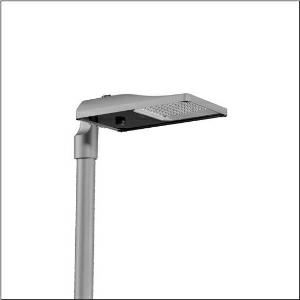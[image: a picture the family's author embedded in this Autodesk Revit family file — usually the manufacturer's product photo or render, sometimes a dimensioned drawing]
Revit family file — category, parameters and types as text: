
# Revit family: streetlight_sl_31_midi___st0_5a_5xh7b4at08la_3b68
name_source: partatom
category: Lighting Fixtures
units: mm (PartAtom-declared; Revit-internal decimal feet)

## family parameters
Cut with Voids When Loaded = No
Host = Face
Light Source = No
Part Type = Normal
Room Calculation Point = No
Round Connector Dimension = Use Diameter
Shared = No

## types (1)
- --- (1 x LED, 13610 lm, 86.5 W, 4000K)
    Apparent Load = 87 VA
    CIE Flux Codes = 41 75 97 100 100
    Color Rendering = 70
    Color Temperature = 4000K
    Default Elevation = 1800 mm
    Description = Streetlight SL 31 midi D4i mast luminaire for post-top, side-entry; light control with lens of PMMA; light distribution: ST0.5a, direct asymmetric distribution, for standard-compliant lighting for roads and squares; LED: luminous flux: 13.610lm, light colour: 740, colour temperature: 4000K; luminous efficacy: 157,3lm/W; control: pre-setting: logarithmic dimming characteristic, flexible luminous flux parameterisation, time-dependent luminous flux control, constant luminous flux control, power reduction, intelligent temperature release in ECG and LED module, overheat protection; luminaire housing, of diecast aluminium, Siteco® metallic grey (DB 702S), corrosivity category C5 high according to DIN EN ISO 12944; cover of toughened safety glass, transparent, opened without tools; mast flange of diecast aluminium, Siteco® metallic grey (DB 702S), spigot size: 76/60mm, mast flange included unmounted; with cable H07RN-F 2x 1.5mm², cable length: 10,5m, connection cable pre-assembled; mains connection: 220..240V, AC, 50/60Hz; power consumption (at start of service life): 86,5W / (at end of service life): 90W / (with reduced operation 50%): 39,6W; protection rating (complete): IP66; insulation class (complete): insulation class II (safety insulation); impact resistance: IK09; certification: CE, ENEC, ENEC+, VDE, UKCA, ZD4i; permissible operating ambient temperature for outdoor applications: -40..+50°C; packaging unit: 1 piece

Light Distribution: ST0.5a
    Height = 79 mm
    Lamp = 1 x LED
    Lamp Light Flux = 13610 lm
    Lamp Power = 86.5 W
    Lamp count = 1
    Length = 577 mm
    Luminous efficacy = 157 lm/W
    Manufacturer = Siteco
    ModVariant = No
    Model = 5XH7B4AT08LA
    Number of Poles = 1
    OnlyDefault = Yes
    Power Factor = 1
    Product Name = Streetlight SL 31 midi | ST0.5a
    Product group = mast luminaire | pylon top
    ProductGroupID = 6100
    Protection Class = Protection class II
    Protection Degree = IP 66
    RLX_Detail_Level = 1
    RLX_Emergency_Light_Flux = 0 lm
    RLX_Emergency_Type = 0
    RLX_Emergency_Type_DB = No
    RlxData = <blob elided: 53705 chars, md5=05ab0012>
    Socket = socket
    Standby Power = 0 W
    System Light Flux = 13610 lm
    System Power = 87 W
    Type Comments = factory setting: luminous flux: 100 % | dim-lin: 254 | 456 mA
    Type Image = l_1300321.jpg
    URL = http://relux.com
    VarID = @adj_078109
    Voltage = 0 V
    Weight = 0.00 kg
    Width = 362 mm

## geometry (parser evidence)
native form markers: Blend x4, Sweep x12
no freeform markers — native parametric forms only
